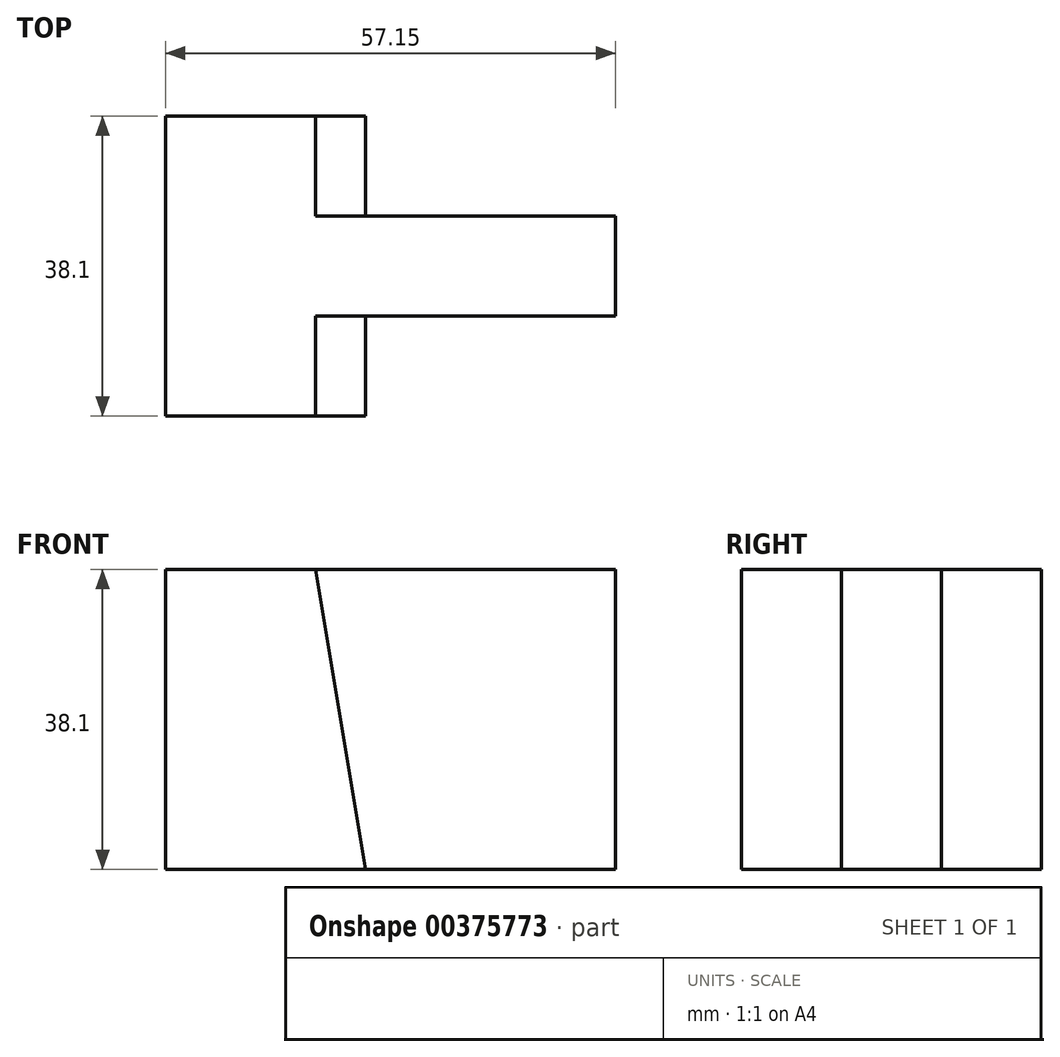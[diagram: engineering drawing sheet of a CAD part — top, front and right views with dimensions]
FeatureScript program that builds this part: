
annotation { "Feature Type Name" : "Feature", "Feature Type Description" : "" }
export const myFeature = defineFeature(function(context is Context, id is Id, definition is map)
    precondition{}
    {
        {
            var Q0;
            Q0=qCreatedBy(makeId("Front.planeOp"),FACE);
            var sketch = newSketch(context, id + "F0", { "sketchPlane" : qUnion([Q0])});
            skLineSegment(sketch, "E0", {"start": v(0, 0) * mm, "end": v(57.15, 0) * mm});
            skLineSegment(sketch, "E1", {"start": v(57.15, 0) * mm, "end": v(57.15, 38.1) * mm});
            skLineSegment(sketch, "E2", {"start": v(57.15, 38.1) * mm, "end": v(0, 38.1) * mm});
            skLineSegment(sketch, "E3", {"start": v(0, 38.1) * mm, "end": v(0, 0) * mm});
            skSolve(sketch);
        }
        {
            var Q0;
            Q0 = qSketchRegion(id + "F0", true);
            extrude(context, id + "F1", {"entities" : qUnion([Q0]), "oppositeDirection" : true, "depth" : 38.1 * mm});
        }
        {
            var Q0;
            Q0=makeQuery(id+"F1.opExtrude","CAP_FACE",FACE,{"disambiguationData":[OSD([sQuery(id+"F0.wireOp",EDGE,"E0"),sQuery(id+"F0.wireOp",EDGE,"E1"),sQuery(id+"F0.wireOp",EDGE,"E2"),sQuery(id+"F0.wireOp",EDGE,"E3")])],"isStart":true});
            var sketch = newSketch(context, id + "F2", { "sketchPlane" : qUnion([Q0])});
            skLineSegment(sketch, "E4", {"start": v(19.05, 38.1) * mm, "end": v(25.4, 0) * mm});
            skSolve(sketch);
        }
        {
            var Q0;
            Q0 = qSketchRegion(id + "F2", true);
            var Q1;
            {var subQ0=sQuery(id+"F2.wireOp",EDGE,"E4");Q1=makeQuery(id+"F2.imprint","IMPRINT",FACE,{"disambiguationData":[TD([[makeQuery(id+"F2.imprint","IMPRINT",EDGE,{"derivedFrom":subQ0}),1.0]])]});}
            extrude(context, id + "F3", {"entities" : qUnion([Q0, Q1]), "operationType" : NewBodyOperationType.REMOVE, "oppositeDirection" : true, "depth" : 12.7 * mm});
        }
        {
            var Q0;
            Q0=makeQuery(id+"F1.opExtrude","CAP_FACE",FACE,{"disambiguationData":[OSD([sQuery(id+"F0.wireOp",EDGE,"E0"),sQuery(id+"F0.wireOp",EDGE,"E1"),sQuery(id+"F0.wireOp",EDGE,"E2"),sQuery(id+"F0.wireOp",EDGE,"E3")])],"isStart":false});
            var sketch = newSketch(context, id + "F4", { "sketchPlane" : qUnion([Q0])});
            skLineSegment(sketch, "E5", {"start": v(-19.05, 38.1) * mm, "end": v(-25.4, 0) * mm});
            skSolve(sketch);
        }
        {
            var Q0;
            {var subQ0=sQuery(id+"F4.wireOp",EDGE,"E5");Q0=makeQuery(id+"F4.imprint","IMPRINT",FACE,{"disambiguationData":[TD([[makeQuery(id+"F4.imprint","IMPRINT",EDGE,{"derivedFrom":subQ0}),-1.0]])]});}
            extrude(context, id + "F5", {"entities" : qUnion([Q0]), "operationType" : NewBodyOperationType.REMOVE, "oppositeDirection" : true, "depth" : 12.7 * mm});
        }
    });
